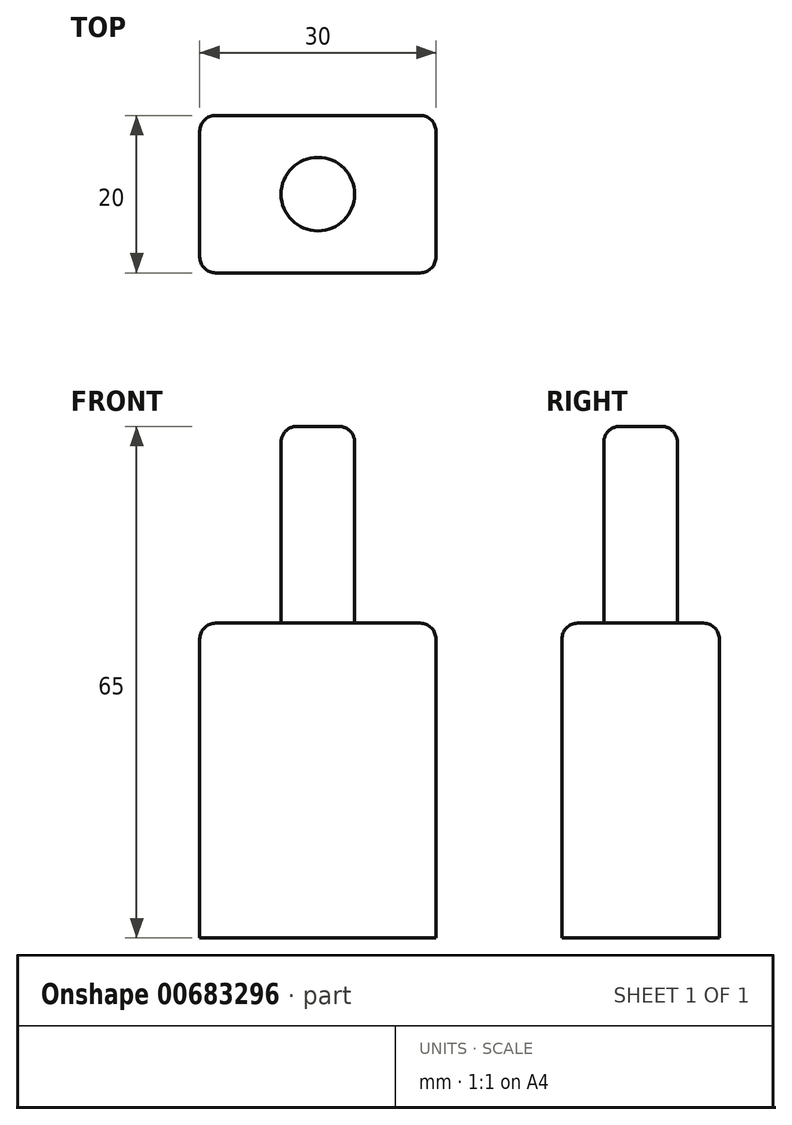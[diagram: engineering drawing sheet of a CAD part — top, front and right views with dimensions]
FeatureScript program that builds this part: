
annotation { "Feature Type Name" : "Feature", "Feature Type Description" : "" }
export const myFeature = defineFeature(function(context is Context, id is Id, definition is map)
    precondition{}
    {
        {
            var Q0;
            Q0=qCreatedBy(makeId("Top.planeOp"),FACE);
            var sketch = newSketch(context, id + "F0", { "sketchPlane" : qUnion([Q0])});
            skLineSegment(sketch, "E0.bottom", {"start": v(0, 0) * mm, "end": v(30, 0) * mm});
            skLineSegment(sketch, "E0.top", {"start": v(0, 20) * mm, "end": v(30, 20) * mm});
            skLineSegment(sketch, "E0.left", {"start": v(0, 0) * mm, "end": v(0, 20) * mm});
            skLineSegment(sketch, "E0.right", {"start": v(30, 0) * mm, "end": v(30, 20) * mm});
            skSolve(sketch);
        }
        {
            var Q0;
            Q0 = qSketchRegion(id + "F0", true);
            extrude(context, id + "F1", {"entities" : qUnion([Q0]), "depth" : 40 * mm, "offsetDistance" : 25 * mm});
        }
        {
            var Q0;
            Q0=makeQuery(id+"F1.opExtrude","CAP_FACE",FACE,{"disambiguationData":[OSD([sQuery(id+"F0.wireOp",EDGE,"E0.bottom"),sQuery(id+"F0.wireOp",EDGE,"E0.top"),sQuery(id+"F0.wireOp",EDGE,"E0.left"),sQuery(id+"F0.wireOp",EDGE,"E0.right")])],"isStart":false});
            var sketch = newSketch(context, id + "F2", { "sketchPlane" : qUnion([Q0])});
            skCircle(sketch, "E1", {"center": v(15, 10) * mm, "radius": 4.67 * mm});
            skSolve(sketch);
        }
        {
            var Q0;
            Q0 = qSketchRegion(id + "F2", true);
            extrude(context, id + "F3", {"entities" : qUnion([Q0]), "operationType" : NewBodyOperationType.ADD, "depth" : 25 * mm, "offsetDistance" : 25 * mm});
        }
        {
            var Q0;
            Q0=makeQuery(id+"F3.opExtrude","CAP_EDGE",EDGE,{"disambiguationData":[OSD([sQuery(id+"F2.wireOp",EDGE,"E1")])],"isStart":false});
            var Q1;
            Q1=makeQuery(id+"F1.opExtrude","CAP_EDGE",EDGE,{"disambiguationData":[OSD([sQuery(id+"F0.wireOp",EDGE,"E0.right")])],"isStart":false});
            var Q2;
            Q2=makeQuery(id+"F1.opExtrude","CAP_EDGE",EDGE,{"disambiguationData":[OSD([sQuery(id+"F0.wireOp",EDGE,"E0.bottom")])],"isStart":false});
            var Q3;
            Q3=makeQuery(id+"F1.opExtrude","CAP_EDGE",EDGE,{"disambiguationData":[OSD([sQuery(id+"F0.wireOp",EDGE,"E0.left")])],"isStart":false});
            var Q4;
            Q4=makeQuery(id+"F1.opExtrude","CAP_EDGE",EDGE,{"disambiguationData":[OSD([sQuery(id+"F0.wireOp",EDGE,"E0.top")])],"isStart":false});
            var Q5;
            Q5=makeQuery(id+"F1.opExtrude","SWEPT_EDGE",EDGE,{"disambiguationData":[OSD([sQuery(id+"F0.wireOp",EDGE,"E0.top"),sQuery(id+"F0.wireOp",EDGE,"E0.right")])]});
            var Q6;
            Q6=makeQuery(id+"F1.opExtrude","SWEPT_EDGE",EDGE,{"disambiguationData":[OSD([sQuery(id+"F0.wireOp",EDGE,"E0.bottom"),sQuery(id+"F0.wireOp",EDGE,"E0.right")])]});
            var Q7;
            Q7=makeQuery(id+"F1.opExtrude","SWEPT_EDGE",EDGE,{"disambiguationData":[OSD([sQuery(id+"F0.wireOp",EDGE,"E0.bottom"),sQuery(id+"F0.wireOp",EDGE,"E0.left")])]});
            var Q8;
            Q8=makeQuery(id+"F1.opExtrude","SWEPT_EDGE",EDGE,{"disambiguationData":[OSD([sQuery(id+"F0.wireOp",EDGE,"E0.top"),sQuery(id+"F0.wireOp",EDGE,"E0.left")])]});
            fillet(context, id + "F4", {"entities" : qUnion([Q0, Q1, Q2, Q3, Q4, Q5, Q6, Q7, Q8]), "radius" : 2 * mm, "tangentPropagation" : true, "allowEdgeOverflow" : false});
        }
    });
